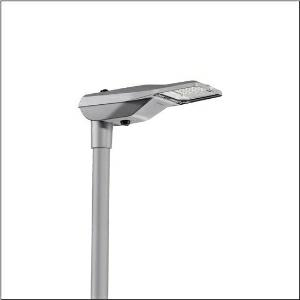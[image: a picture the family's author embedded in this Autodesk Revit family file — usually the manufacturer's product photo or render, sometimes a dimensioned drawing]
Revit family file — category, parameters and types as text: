
# Revit family: streetlight_sl_21_iq_micro___p0_5a_5xe1v31y08db_c8d5
name_source: partatom
category: Lighting Fixtures
units: mm (PartAtom-declared; Revit-internal decimal feet)

## family parameters
Cut with Voids When Loaded = No
Host = Face
Light Source = No
Part Type = Normal
Room Calculation Point = No
Round Connector Dimension = Use Diameter
Shared = No

## types (1)
- --- (1 x LED, 5030 lm, 39.1 W, 3000K)
    Apparent Load = 39 VA
    CIE Flux Codes = 37 73 96 100 100
    Color Rendering = 70
    Color Temperature = 3000K
    Default Elevation = 1800 mm
    Description = Streetlight SL 21 iQ micro, mast luminaire, primary light control with lens, of PMMA, primary optical cover: cover, of toughened safety glass, transparent, light distribution: P0.5a, light emission: direct distribution, primary light characteristic: asymmetric, installation type: post-top, side-entry, LED, High Power LED, rated luminous flux: 5.030lm, luminous efficacy: 129lm/W, light colour: 730, colour temperature: 3000K, control gear: iQ-Street Remote, D4i with power reduction, control: pre-setting: logarithmic dimming characteristic, Street-Remote, Auto-Match, Temp-Guard, Lumen-Switch, Night-Set, Smart-Wire, Light-Fading, Desk-Remote (wireless, voltage-free reading and setting of iQ features in the workshop via application-optimized NFC function/RFID function), optimised constant luminous flux control (CLO 2.0), mains connection: 220..240V, AC, 50/60Hz, start of lifetime: 39W, end of service life: 41W, reduction: 17W, luminaire housing, of diecast aluminium, powder-coated, Siteco® metallic grey (DB 702S), corrosivity category C5 mid according to DIN EN ISO 12944, please order mast flange separately, inclination adjustable: 0°, 5°, 10°, 15°, sealing non-destructively replaceable, multi-level sealing system, length: 528mm, width: 235mm, height: 110mm, mast flange for spigot size: 42mm (side-entry): 5XC10008XM4, 60/48mm (side-entry/post-top): 5XC10108XM2, 76/60mm (side-entry/post-top): 5XC10108XM1, mounting height: 4..8m, Smart Interface below and above, protection rating (complete): IP66, insulation class (complete): insulation class II (safety insulation), certification: CE, ENEC, ENEC+, VDE, impact resistance: IK10, permissible operating ambient temperature for outdoor applications: -40..+50°C, standard-compliant lighting for roads and squares, packaging unit: 1 piece

Light Distribution: P0.5a
    Height = 110 mm
    Lamp = 1 x LED
    Lamp Light Flux = 5030 lm
    Lamp Power = 39.1 W
    Lamp count = 1
    Length = 528 mm
    Luminous efficacy = 129 lm/W
    Manufacturer = Siteco
    ModVariant = No
    Model = 5XE1V31Y08DB
    Number of Poles = 1
    OnlyDefault = Yes
    Power Factor = 1
    Product Name = Streetlight SL 21 iQ micro | P0.5a
    Product group = mast luminaire | pylon top
    ProductGroupID = 6100
    Protection Class = Protection class II
    Protection Degree = IP 66
    RLX_Detail_Level = 1
    RLX_Emergency_Light_Flux = 0 lm
    RLX_Emergency_Type = 0
    RLX_Emergency_Type_DB = No
    RlxData = <blob elided: 98237 chars, md5=ab1c38fe>
    Socket = socket
    Standby Power = 0 W
    System Light Flux = 5030 lm
    System Power = 39 W
    Type Comments = factory setting: luminous flux: 100 % | dim-lin: 254 | 765 mA
    Type Image = l_1007239.jpg
    URL = http://relux.com
    VarID = @adj_070790
    Voltage = 0 V
    Weight = 0.00 kg
    Width = 235 mm

## geometry (parser evidence)
native form markers: Blend x4, Sweep x10
no freeform markers — native parametric forms only
